# Revit family: Toilet_Seat-Elongated_Closed_Front-KOHLER-Reach-K-4087X_1
name_source: partatom
category: Specialty Equipment
units: mm (PartAtom-declared; Revit-internal decimal feet)

## family parameters
Cut with Voids When Loaded = No
Host = Face
OmniClass Number = 23.31.19.19.17
OmniClass Title = Water Closet Seats
Part Type = Normal
Room Calculation Point = No
Round Connector Dimension = Use Diameter
Shared = No

## types (1)
- 0-White
    ADA Compliant = No
    Assembly Code = C1030200
    Date Modified = 12/16/2022
    Default Elevation = 15"
    Description = Quiet-Close Seat, Hidden Hinge Bas
    Finish = Kohler-Plastic-0-White
    Height = 2 5/8"
    Length = 19 13/16"
    Manufacturer = Kohler Co.
    Master Format 2014 = 10 28 00
    Master Format 2014 Name = Toilet, Bath, and Laundry Accessories
    Material = Plastic
    Model = K-4087X-0
    Product Name = Reach
    Type = 1
    URL = https://www.kohler.co.th
    WaterSense Certified = No
    Width = 14 3/8"

## geometry (parser evidence)
native form markers: Sweep x6
no freeform markers — native parametric forms only
